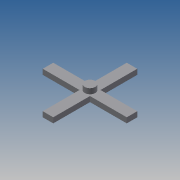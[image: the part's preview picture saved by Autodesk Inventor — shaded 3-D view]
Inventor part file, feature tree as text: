
AUTODESK INVENTOR PART (.ipt)
format: ipt  version: 2014 SP1 (Build 180222100, 222)  size: 89,088 bytes
history: native  units: in
note: dims shown in document units (in); Inventor stores cm internally (conversion verified against a paired STEP export)
features: extrude x2, sketch x2
ambient origin geometry x8: Origin, YZ Plane, XZ Plane, XY Plane, X Axis, Y Axis, Z Axis, Center Point
bodies: Solid1 (feature_tree)
feature tree (4):
  extrude  "Extrusion1"  Depth=1.0in
  extrude  "Extrusion2"  Depth=8.0in
  sketch  "Sketch1"  dims[d0=8.0in d1=1.0in]
  sketch  "Sketch2"  dims[d2=1.0in d3=8.0in d4=0.5in d5=0.0in d7=1.0in d8=0.5in d9=0.0in]
